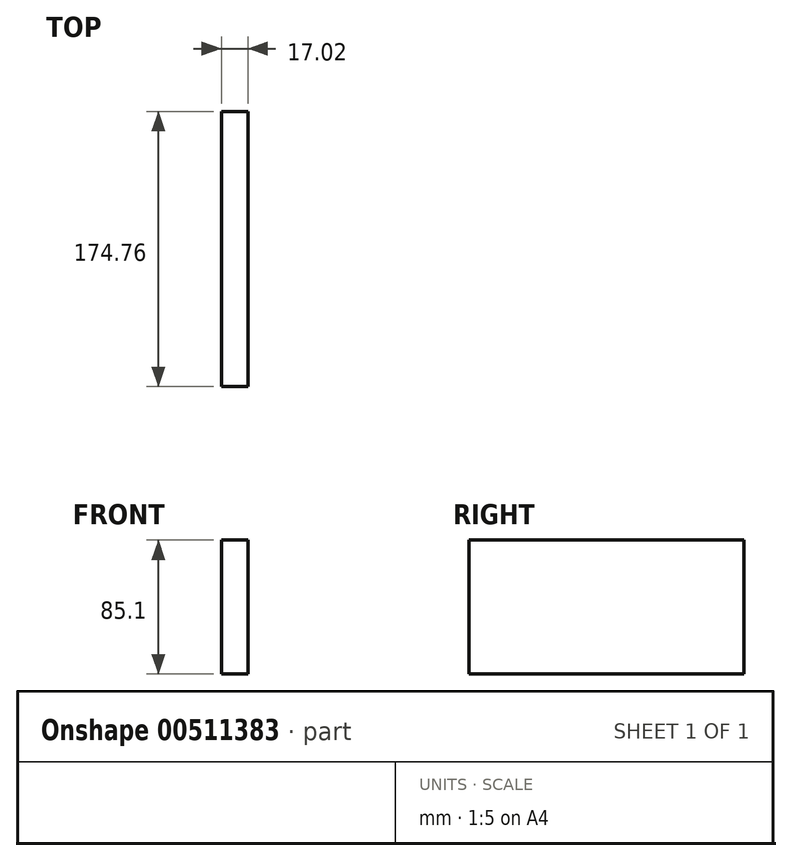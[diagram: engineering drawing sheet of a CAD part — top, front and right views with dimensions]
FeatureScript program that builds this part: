
annotation { "Feature Type Name" : "Feature", "Feature Type Description" : "" }
export const myFeature = defineFeature(function(context is Context, id is Id, definition is map)
    precondition{}
    {
        {
            var Q0;
            Q0=qCreatedBy(makeId("Right.planeOp"),FACE);
            var sketch = newSketch(context, id + "F0", { "sketchPlane" : qUnion([Q0])});
            skLineSegment(sketch, "E0.bottom", {"start": v(-87.38, 42.55) * mm, "end": v(87.38, 42.55) * mm});
            skLineSegment(sketch, "E0.top", {"start": v(-87.38, -42.55) * mm, "end": v(87.38, -42.55) * mm});
            skLineSegment(sketch, "E0.left", {"start": v(-87.38, 42.55) * mm, "end": v(-87.38, -42.55) * mm});
            skLineSegment(sketch, "E0.right", {"start": v(87.38, 42.55) * mm, "end": v(87.38, -42.55) * mm});
            skPoint(sketch, "E0.middle", {"position": v(0, 0) * mm});
            skSolve(sketch);
        }
        {
            var Q0;
            Q0=makeQuery(id+"F0.imprint","IMPRINT",FACE,{"disambiguationData":[TD([[makeQuery(id+"F0.imprint","IMPRINT",EDGE,{"derivedFrom":sQuery(id+"F0.wireOp",EDGE,"E0.bottom")}),-1.0]])]});
            extrude(context, id + "F1", {"entities" : qUnion([Q0]), "endBound" : BoundingType.SYMMETRIC, "depth" : 17.02 * mm, "offsetDistance" : 25.4 * mm});
        }
        {
            var Q0;
            Q0=makeQuery(id+"F1.opExtrude","CAP_FACE",FACE,{"disambiguationData":[OSD([sQuery(id+"F0.wireOp",EDGE,"E0.bottom"),sQuery(id+"F0.wireOp",EDGE,"E0.top"),sQuery(id+"F0.wireOp",EDGE,"E0.left"),sQuery(id+"F0.wireOp",EDGE,"E0.right")])],"isStart":false});
            var sketch = newSketch(context, id + "F2", { "sketchPlane" : qUnion([Q0])});
            skLineSegment(sketch, "E1.bottom", {"start": v(-87.38, 1.4) * mm, "end": v(-47.5, 1.4) * mm});
            skLineSegment(sketch, "E1.top", {"start": v(-87.38, 13.33) * mm, "end": v(-47.5, 13.33) * mm});
            skLineSegment(sketch, "E1.left", {"start": v(-87.38, 1.4) * mm, "end": v(-87.38, 13.33) * mm});
            skLineSegment(sketch, "E1.right", {"start": v(-47.5, 1.4) * mm, "end": v(-47.5, 13.33) * mm});
            skLineSegment(sketch, "E2.bottom", {"start": v(47.5, 1.4) * mm, "end": v(87.38, 1.4) * mm});
            skLineSegment(sketch, "E2.top", {"start": v(47.5, 13.33) * mm, "end": v(87.38, 13.33) * mm});
            skLineSegment(sketch, "E2.left", {"start": v(47.5, 1.4) * mm, "end": v(47.5, 13.33) * mm});
            skLineSegment(sketch, "E2.right", {"start": v(87.38, 1.4) * mm, "end": v(87.38, 13.33) * mm});
            skSolve(sketch);
        }
        {
            var Q0;
            Q0=makeQuery(id+"F1.opExtrude","CAP_FACE",FACE,{"disambiguationData":[OSD([sQuery(id+"F0.wireOp",EDGE,"E0.bottom"),sQuery(id+"F0.wireOp",EDGE,"E0.top"),sQuery(id+"F0.wireOp",EDGE,"E0.left"),sQuery(id+"F0.wireOp",EDGE,"E0.right")])],"isStart":true});
            var sketch = newSketch(context, id + "F3", { "sketchPlane" : qUnion([Q0])});
            skLineSegment(sketch, "E3.bottom", {"start": v(-87.38, 1.4) * mm, "end": v(-47.5, 1.4) * mm});
            skLineSegment(sketch, "E3.top", {"start": v(-87.38, 13.33) * mm, "end": v(-47.5, 13.34) * mm});
            skLineSegment(sketch, "E3.left", {"start": v(-87.38, 1.4) * mm, "end": v(-87.38, 13.33) * mm});
            skLineSegment(sketch, "E3.right", {"start": v(-47.5, 1.4) * mm, "end": v(-47.5, 13.34) * mm});
            skLineSegment(sketch, "E4.bottom", {"start": v(47.5, 1.4) * mm, "end": v(87.38, 1.4) * mm});
            skLineSegment(sketch, "E4.top", {"start": v(47.5, 13.33) * mm, "end": v(87.38, 13.34) * mm});
            skLineSegment(sketch, "E4.left", {"start": v(47.5, 1.4) * mm, "end": v(47.5, 13.33) * mm});
            skLineSegment(sketch, "E4.right", {"start": v(87.38, 1.4) * mm, "end": v(87.38, 13.34) * mm});
            skSolve(sketch);
        }
    });
